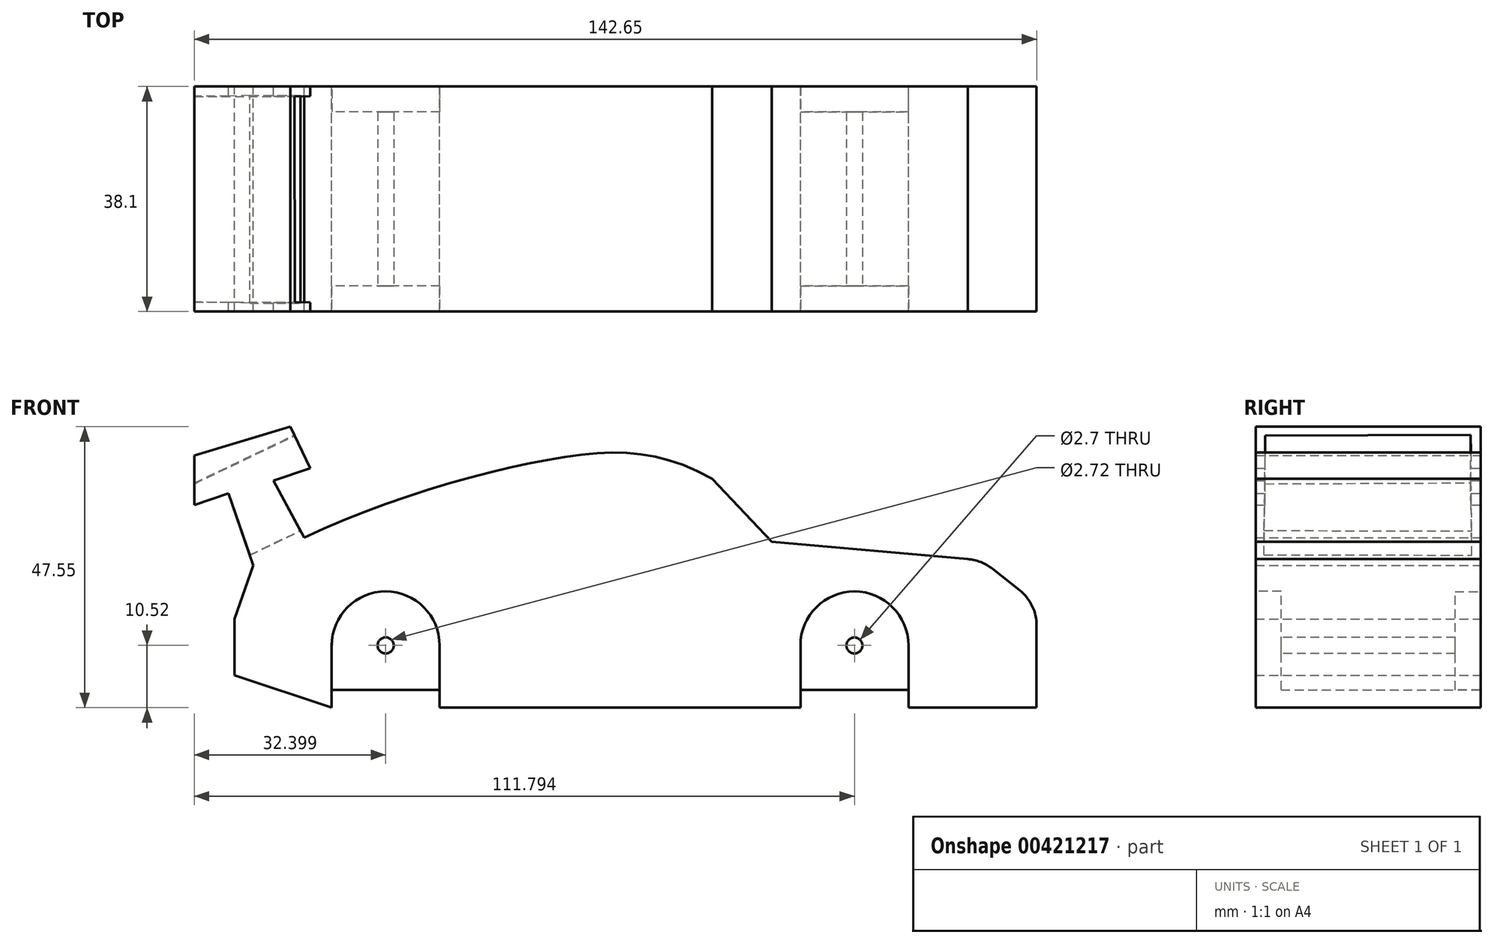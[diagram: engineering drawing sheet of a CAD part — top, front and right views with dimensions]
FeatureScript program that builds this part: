
annotation { "Feature Type Name" : "Feature", "Feature Type Description" : "" }
export const myFeature = defineFeature(function(context is Context, id is Id, definition is map)
    precondition{}
    {
        {
            var Q0;
            Q0=qCreatedBy(makeId("Front.planeOp"),FACE);
            var sketch = newSketch(context, id + "F0", { "sketchPlane" : qUnion([Q0])});
            skLineSegment(sketch, "E0", {"start": v(47.44, 13) * mm, "end": v(52.03, 9.36) * mm});
            skLineSegment(sketch, "E1", {"start": v(54.93, 3.38) * mm, "end": v(54.93, -10.52) * mm});
            skLineSegment(sketch, "E2", {"start": v(54.93, -10.52) * mm, "end": v(33.22, -10.52) * mm});
            skLineSegment(sketch, "E3", {"start": v(33.22, -10.52) * mm, "end": v(33.22, 0) * mm});
            skPoint(sketch, "E4.visualSharp", {"position": v(47.05, 13.3) * mm});
            skArc(sketch, "E4.filletArc", {"start": v(47.44, 13) * mm, "mid": v(45.47, 14.12) * mm, "end": v(43.27, 14.62) * mm});
            skPoint(sketch, "E5.visualSharp", {"position": v(54.93, 7.07) * mm});
            skArc(sketch, "E5.filletArc", {"start": v(54.93, 3.38) * mm, "mid": v(54.17, 6.7) * mm, "end": v(52.03, 9.36) * mm});
            skArc(sketch, "E6", {"start": v(33.22, 0) * mm, "mid": v(24.08, 9.15) * mm, "end": v(14.93, 0) * mm});
            skLineSegment(sketch, "E7", {"start": v(14.93, 0) * mm, "end": v(14.93, -10.52) * mm});
            skLineSegment(sketch, "E8", {"start": v(43.27, 14.62) * mm, "end": v(10.06, 17.53) * mm});
            skLineSegment(sketch, "E9", {"start": v(14.93, -7.5) * mm, "end": v(33.22, -7.5) * mm});
            skLineSegment(sketch, "E10", {"start": v(10.06, 17.53) * mm, "end": v(0, 28.2) * mm});
            skFitSpline(sketch, "E11", {"points": [v(0, 28.2) * mm, v(-27.13, 31.55) * mm, v(-77.72, 13.56) * mm], "startDerivative": vector(-65.57, 36.72) * mm, "endDerivative": vector(-73.64, -45.44) * mm});
            skLineSegment(sketch, "E12", {"start": v(14.93, -10.52) * mm, "end": v(-46.18, -10.52) * mm});
            skLineSegment(sketch, "E13", {"start": v(-46.18, -10.52) * mm, "end": v(-46.18, 0) * mm});
            skLineSegment(sketch, "E14", {"start": v(-64.47, -10.52) * mm, "end": v(-64.47, 0) * mm});
            skArc(sketch, "E15", {"start": v(-46.18, 0) * mm, "mid": v(-55.32, 9.14) * mm, "end": v(-64.47, 0) * mm});
            skLineSegment(sketch, "E16", {"start": v(-77.72, 13.56) * mm, "end": v(-80.92, 4.47) * mm});
            skLineSegment(sketch, "E17", {"start": v(-80.92, 4.47) * mm, "end": v(-80.92, -5.03) * mm});
            skLineSegment(sketch, "E18", {"start": v(-80.92, -5.03) * mm, "end": v(-64.47, -10.52) * mm});
            skLineSegment(sketch, "E19", {"start": v(-46.18, -7.5) * mm, "end": v(-64.47, -7.5) * mm});
            skPoint(sketch, "E20.endSnap0", {"position": v(-69.13, 23.73) * mm});
            skPoint(sketch, "E21.orphan", {"position": v(-66.9, 19.27) * mm});
            skLineSegment(sketch, "E22", {"start": v(-69.13, 18.23) * mm, "end": v(-74.3, 27.89) * mm});
            skLineSegment(sketch, "E23", {"start": v(-77.72, 13.56) * mm, "end": v(-81.91, 25.76) * mm});
            skLineSegment(sketch, "E24", {"start": v(-81.91, 25.76) * mm, "end": v(-74.3, 27.89) * mm});
            skLineSegment(sketch, "E25", {"start": v(-74.3, 27.89) * mm, "end": v(-68.09, 30.02) * mm});
            skLineSegment(sketch, "E26", {"start": v(-81.91, 25.76) * mm, "end": v(-87.72, 23.76) * mm});
            skLineSegment(sketch, "E27", {"start": v(-87.72, 23.76) * mm, "end": v(-87.72, 32.16) * mm});
            skLineSegment(sketch, "E28", {"start": v(-87.72, 32.16) * mm, "end": v(-71.44, 37.03) * mm});
            skLineSegment(sketch, "E29", {"start": v(-71.44, 37.03) * mm, "end": v(-68.09, 30.02) * mm});
            skSolve(sketch);
        }
        {
            var Q0;
            Q0 = qSketchRegion(id + "F0", true);
            extrude(context, id + "F1", {"entities" : qUnion([Q0]), "depth" : 38.1 * mm});
        }
        {
            var Q0;
            Q0=makeQuery(id+"F1.opExtrude","SWEPT_FACE",FACE,{"disambiguationData":[OSD([sQuery(id+"F0.wireOp",EDGE,"E29")])]});
            var sketch = newSketch(context, id + "F2", { "sketchPlane" : qUnion([Q0])});
            skLineSegment(sketch, "E30", {"start": v(-1.5, 47.58) * mm, "end": v(-36.68, 47.65) * mm});
            skLineSegment(sketch, "E31", {"start": v(-1.7, 62.68) * mm, "end": v(-36.48, 62.53) * mm});
            skLineSegment(sketch, "E32", {"start": v(-36.48, 62.53) * mm, "end": v(-36.68, 47.65) * mm});
            skLineSegment(sketch, "E33", {"start": v(-1.7, 62.68) * mm, "end": v(-1.5, 47.58) * mm});
            skSolve(sketch);
        }
        {
            var Q0;
            Q0 = qSketchRegion(id + "F2", true);
            var Q1;
            Q1 = qSketchRegion(id + "F4", true);
            extrude(context, id + "F3", {"entities" : qUnion([Q0, Q1]), "operationType" : NewBodyOperationType.REMOVE, "oppositeDirection" : true, "depth" : 25.4 * mm});
        }
        {
            var Q0;
            Q0=makeQuery(id+"F1.opExtrude","CAP_FACE",FACE,{"disambiguationData":[OSD([sQuery(id+"F0.wireOp",EDGE,"E0"),sQuery(id+"F0.wireOp",EDGE,"E1"),sQuery(id+"F0.wireOp",EDGE,"E2"),sQuery(id+"F0.wireOp",EDGE,"E3"),sQuery(id+"F0.wireOp",EDGE,"E4.filletArc"),sQuery(id+"F0.wireOp",EDGE,"E5.filletArc"),sQuery(id+"F0.wireOp",EDGE,"E7"),sQuery(id+"F0.wireOp",EDGE,"E8"),sQuery(id+"F0.wireOp",EDGE,"E9"),sQuery(id+"F0.wireOp",EDGE,"E10"),sQuery(id+"F0.wireOp",EDGE,"E11"),sQuery(id+"F0.wireOp",EDGE,"E12"),sQuery(id+"F0.wireOp",EDGE,"E13"),sQuery(id+"F0.wireOp",EDGE,"E14"),sQuery(id+"F0.wireOp",EDGE,"E16"),sQuery(id+"F0.wireOp",EDGE,"E17"),sQuery(id+"F0.wireOp",EDGE,"E18"),sQuery(id+"F0.wireOp",EDGE,"E19"),sQuery(id+"F0.wireOp",EDGE,"E22"),sQuery(id+"F0.wireOp",EDGE,"E23"),sQuery(id+"F0.wireOp",EDGE,"E25"),sQuery(id+"F0.wireOp",EDGE,"E26"),sQuery(id+"F0.wireOp",EDGE,"E27"),sQuery(id+"F0.wireOp",EDGE,"E28"),sQuery(id+"F0.wireOp",EDGE,"E29")])],"isStart":true});
            var sketch = newSketch(context, id + "F4", { "sketchPlane" : qUnion([Q0])});
            skCircle(sketch, "E34", {"center": v(56.4, 0) * mm, "radius": 1.6 * mm});
            skCircle(sketch, "E35", {"center": v(-24.53, 0) * mm, "radius": 1.5 * mm});
            skSolve(sketch);
        }
        {
            var Q0;
            Q0=makeQuery(id+"F1.opExtrude","CAP_FACE",FACE,{"disambiguationData":[OSD([sQuery(id+"F0.wireOp",EDGE,"E0"),sQuery(id+"F0.wireOp",EDGE,"E1"),sQuery(id+"F0.wireOp",EDGE,"E2"),sQuery(id+"F0.wireOp",EDGE,"E3"),sQuery(id+"F0.wireOp",EDGE,"E4.filletArc"),sQuery(id+"F0.wireOp",EDGE,"E5.filletArc"),sQuery(id+"F0.wireOp",EDGE,"E7"),sQuery(id+"F0.wireOp",EDGE,"E8"),sQuery(id+"F0.wireOp",EDGE,"E9"),sQuery(id+"F0.wireOp",EDGE,"E10"),sQuery(id+"F0.wireOp",EDGE,"E11"),sQuery(id+"F0.wireOp",EDGE,"E12"),sQuery(id+"F0.wireOp",EDGE,"E13"),sQuery(id+"F0.wireOp",EDGE,"E14"),sQuery(id+"F0.wireOp",EDGE,"E16"),sQuery(id+"F0.wireOp",EDGE,"E17"),sQuery(id+"F0.wireOp",EDGE,"E18"),sQuery(id+"F0.wireOp",EDGE,"E19"),sQuery(id+"F0.wireOp",EDGE,"E22"),sQuery(id+"F0.wireOp",EDGE,"E23"),sQuery(id+"F0.wireOp",EDGE,"E25"),sQuery(id+"F0.wireOp",EDGE,"E26"),sQuery(id+"F0.wireOp",EDGE,"E27"),sQuery(id+"F0.wireOp",EDGE,"E28"),sQuery(id+"F0.wireOp",EDGE,"E29")])],"isStart":false});
            var sketch = newSketch(context, id + "F5", { "sketchPlane" : qUnion([Q0])});
            skLineSegment(sketch, "E36", {"start": v(-64.47, -7.5) * mm, "end": v(-46.18, -7.5) * mm});
            skLineSegment(sketch, "E37", {"start": v(-46.18, -7.5) * mm, "end": v(-46.18, 0) * mm});
            skLineSegment(sketch, "E38", {"start": v(-64.47, -7.5) * mm, "end": v(-64.47, 0) * mm});
            skArc(sketch, "E39", {"start": v(-46.18, 0) * mm, "mid": v(-55.32, 9.14) * mm, "end": v(-64.47, 0) * mm});
            skLineSegment(sketch, "E40", {"start": v(14.93, -7.5) * mm, "end": v(33.22, -7.5) * mm});
            skLineSegment(sketch, "E41", {"start": v(33.22, -7.5) * mm, "end": v(33.22, 0) * mm});
            skLineSegment(sketch, "E42", {"start": v(14.93, -7.5) * mm, "end": v(14.93, 0) * mm});
            skArc(sketch, "E43", {"start": v(33.22, 0) * mm, "mid": v(24.08, 9.15) * mm, "end": v(14.93, 0) * mm});
            skSolve(sketch);
        }
        {
            var Q0;
            Q0 = qSketchRegion(id + "F5", true);
            extrude(context, id + "F6", {"entities" : qUnion([Q0]), "operationType" : NewBodyOperationType.REMOVE, "oppositeDirection" : true, "depth" : 4.32 * mm});
        }
        {
            var Q0;
            Q0=makeQuery(id+"F0.imprint","IMPRINT",FACE,{"disambiguationData":[TD([[makeQuery(id+"F0.imprint","IMPRINT",EDGE,{"derivedFrom":sQuery(id+"F0.wireOp",EDGE,"E0")}),-1.0]])]});
            var sketch = newSketch(context, id + "F7", { "sketchPlane" : qUnion([Q0])});
            skLineSegment(sketch, "E44", {"start": v(33.22, -8.4) * mm, "end": v(14.96, -8.4) * mm});
            skLineSegment(sketch, "E45", {"start": v(14.96, -8.4) * mm, "end": v(14.96, 0) * mm});
            skLineSegment(sketch, "E46", {"start": v(33.22, -8.4) * mm, "end": v(33.22, 0) * mm});
            skArc(sketch, "E47", {"start": v(33.22, 0) * mm, "mid": v(24.1, 9.13) * mm, "end": v(14.96, 0) * mm});
            skLineSegment(sketch, "E48", {"start": v(-46.15, -7.53) * mm, "end": v(-64.38, -7.53) * mm});
            skLineSegment(sketch, "E49", {"start": v(-64.38, -7.53) * mm, "end": v(-64.38, 0) * mm});
            skLineSegment(sketch, "E50", {"start": v(-46.15, -7.53) * mm, "end": v(-46.15, 0) * mm});
            skArc(sketch, "E51", {"start": v(-46.15, 0) * mm, "mid": v(-55.26, 9.12) * mm, "end": v(-64.38, 0) * mm});
            skSolve(sketch);
        }
        {
            var Q0;
            Q0 = qSketchRegion(id + "F7", true);
            extrude(context, id + "F8", {"entities" : qUnion([Q0]), "operationType" : NewBodyOperationType.REMOVE, "depth" : 4.32 * mm});
        }
        {
            var Q0;
            Q0=makeQuery(id+"F6.boolean.opBoolean","COPY",FACE,{"derivedFrom":makeQuery(id+"F6.opExtrude","CAP_FACE",FACE,{"disambiguationData":[OSD([sQuery(id+"F5.wireOp",EDGE,"E36"),sQuery(id+"F5.wireOp",EDGE,"E37"),sQuery(id+"F5.wireOp",EDGE,"E38"),sQuery(id+"F5.wireOp",EDGE,"E39")])],"isStart":false})});
            var sketch = newSketch(context, id + "F9", { "sketchPlane" : qUnion([Q0])});
            skCircle(sketch, "E52", {"center": v(-55.32, 0) * mm, "radius": 1.36 * mm});
            skCircle(sketch, "E53", {"center": v(24.07, 0) * mm, "radius": 1.35 * mm});
            skSolve(sketch);
        }
        {
            var Q0;
            Q0 = qSketchRegion(id + "F9", true);
            extrude(context, id + "F10", {"entities" : qUnion([Q0]), "operationType" : NewBodyOperationType.REMOVE, "oppositeDirection" : true, "depth" : 61.2 * mm});
        }
    });
